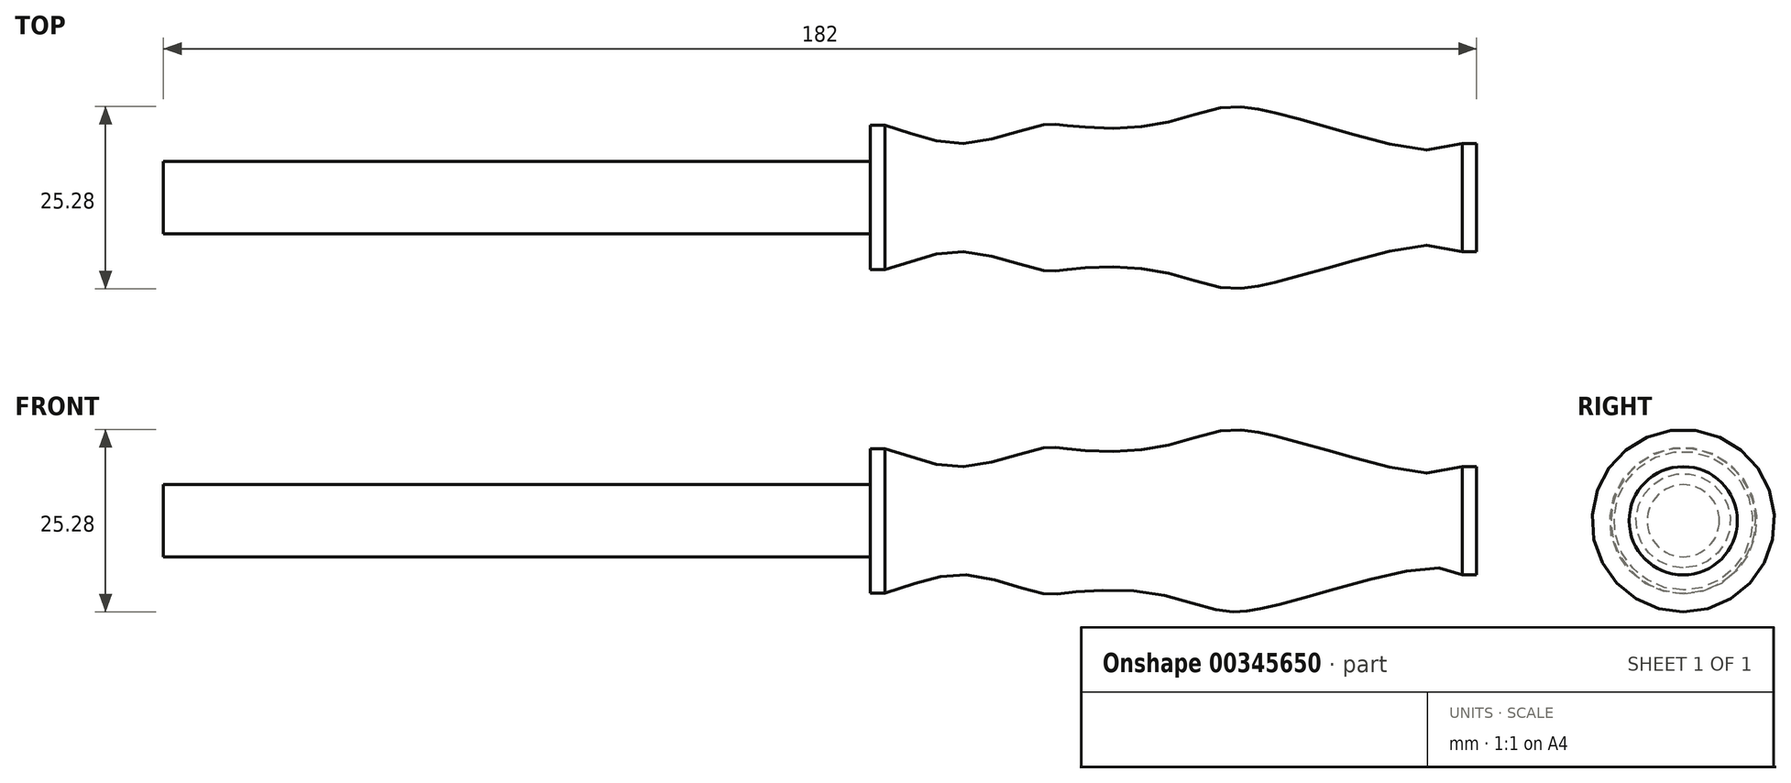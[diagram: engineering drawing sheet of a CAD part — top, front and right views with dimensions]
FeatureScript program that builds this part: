
annotation { "Feature Type Name" : "Feature", "Feature Type Description" : "" }
export const myFeature = defineFeature(function(context is Context, id is Id, definition is map)
    precondition{}
    {
        {
            var Q0;
            Q0=qCreatedBy(makeId("Top.planeOp"),FACE);
            var sketch = newSketch(context, id + "F0", { "sketchPlane" : qUnion([Q0])});
            skLineSegment(sketch, "E0", {"start": v(0, 0) * mm, "end": v(80, 0) * mm});
            skLineSegment(sketch, "E1", {"start": v(50, 0) * mm, "end": v(50, 12.5) * mm, "construction": true});
            skLineSegment(sketch, "E2", {"start": v(25, 0) * mm, "end": v(25, 10) * mm, "construction": true});
            skLineSegment(sketch, "E3", {"start": v(0, 0) * mm, "end": v(0, 10) * mm});
            skLineSegment(sketch, "E4", {"start": v(80, 0) * mm, "end": v(80, 7.5) * mm});
            skFitSpline(sketch, "E5", {"points": [v(80, 7.5) * mm, v(65.4, 8.61) * mm, v(53.22, 11.95) * mm, v(50, 12.5) * mm, v(46.71, 12.5) * mm, v(36.54, 9.95) * mm, v(25, 10) * mm, v(21.53, 10) * mm, v(11.18, 7.5) * mm, v(0, 10) * mm], "startDerivative": vector(-52.63, -41.8) * mm, "endDerivative": vector(-107.14, 31.84) * mm});
            skLineSegment(sketch, "E6", {"start": v(0, 0) * mm, "end": v(-100, 0) * mm});
            skLineSegment(sketch, "E7", {"start": v(-100, 0) * mm, "end": v(-100, 5) * mm});
            skLineSegment(sketch, "E8", {"start": v(0, 10) * mm, "end": v(-2, 10) * mm});
            skLineSegment(sketch, "E9", {"start": v(-2, 10) * mm, "end": v(-2, 0) * mm});
            skLineSegment(sketch, "E10", {"start": v(-100, 5) * mm, "end": v(-2, 5) * mm});
            skLineSegment(sketch, "E11", {"start": v(80, 7.5) * mm, "end": v(82, 7.5) * mm});
            skLineSegment(sketch, "E12", {"start": v(82, 7.5) * mm, "end": v(82, 0) * mm});
            skLineSegment(sketch, "E13", {"start": v(82, 0) * mm, "end": v(80, 0) * mm});
            skSolve(sketch);
        }
        {
            var Q0;
            Q0=makeQuery(id+"F0.imprint","IMPRINT",FACE,{"disambiguationData":[TD([[makeQuery(id+"F0.imprint","IMPRINT",EDGE,{"derivedFrom":sQuery(id+"F0.wireOp",EDGE,"E0")}),1.0]])]});
            var Q1;
            {var subQ4=sQuery(id+"F0.wireOp",EDGE,"E3");Q1=makeQuery(id+"F0.imprint","IMPRINT",FACE,{"disambiguationData":[TD([[makeQuery(id+"F0.imprint","IMPRINT",EDGE,{"derivedFrom":subQ4}),1.0]])]});}
            var Q2;
            {var subQ0=sQuery(id+"F0.wireOp",EDGE,"E7");Q2=makeQuery(id+"F0.imprint","IMPRINT",FACE,{"disambiguationData":[TD([[makeQuery(id+"F0.imprint","IMPRINT",EDGE,{"derivedFrom":subQ0}),-1.0]])]});}
            var Q3;
            Q3=makeQuery(id+"F0.imprint","IMPRINT",FACE,{"disambiguationData":[TD([[makeQuery(id+"F0.imprint","IMPRINT",EDGE,{"derivedFrom":sQuery(id+"F0.wireOp",EDGE,"E4")}),-1.0]])]});
            var Q4;
            Q4=sQuery(id+"F0.wireOp",EDGE,"E6");
            revolve(context, id + "F1", {"entities" : qUnion([Q0, Q1, Q2, Q3]), "axis" : qUnion([Q4]), "revolveType" : RevolveType.FULL});
        }
    });
